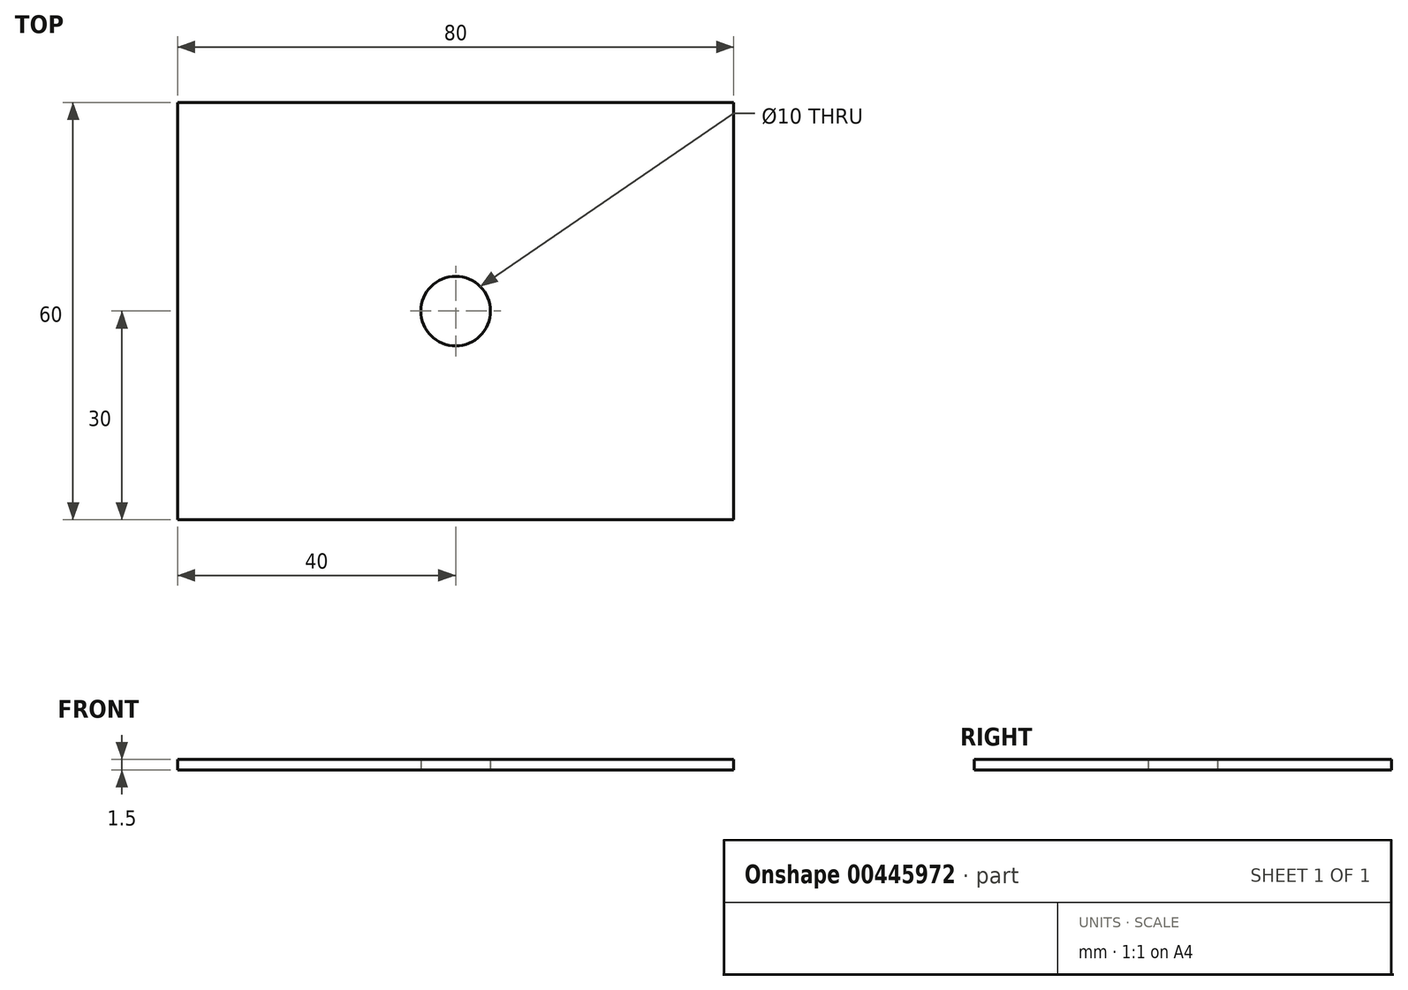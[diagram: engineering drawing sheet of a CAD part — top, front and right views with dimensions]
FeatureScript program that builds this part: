
annotation { "Feature Type Name" : "Feature", "Feature Type Description" : "" }
export const myFeature = defineFeature(function(context is Context, id is Id, definition is map)
    precondition{}
    {
        {
            var Q0;
            Q0=qCreatedBy(makeId("Top.planeOp"),FACE);
            var sketch = newSketch(context, id + "F0", { "sketchPlane" : qUnion([Q0])});
            skLineSegment(sketch, "E0.bottom", {"start": v(-40, 30) * mm, "end": v(40, 30) * mm});
            skLineSegment(sketch, "E0.top", {"start": v(-40, -30) * mm, "end": v(40, -30) * mm});
            skLineSegment(sketch, "E0.left", {"start": v(-40, 30) * mm, "end": v(-40, -30) * mm});
            skLineSegment(sketch, "E0.right", {"start": v(40, 30) * mm, "end": v(40, -30) * mm});
            skPoint(sketch, "E0.middle", {"position": v(0, 0) * mm});
            skCircle(sketch, "E1", {"center": v(0, 0) * mm, "radius": 5 * mm});
            skSolve(sketch);
        }
        {
            var Q0;
            Q0=qSketchRegion(id+"F0",true);
            extrude(context, id + "F1", {"entities" : qUnion([Q0]), "depth" : 1.5 * mm});
        }
    });
